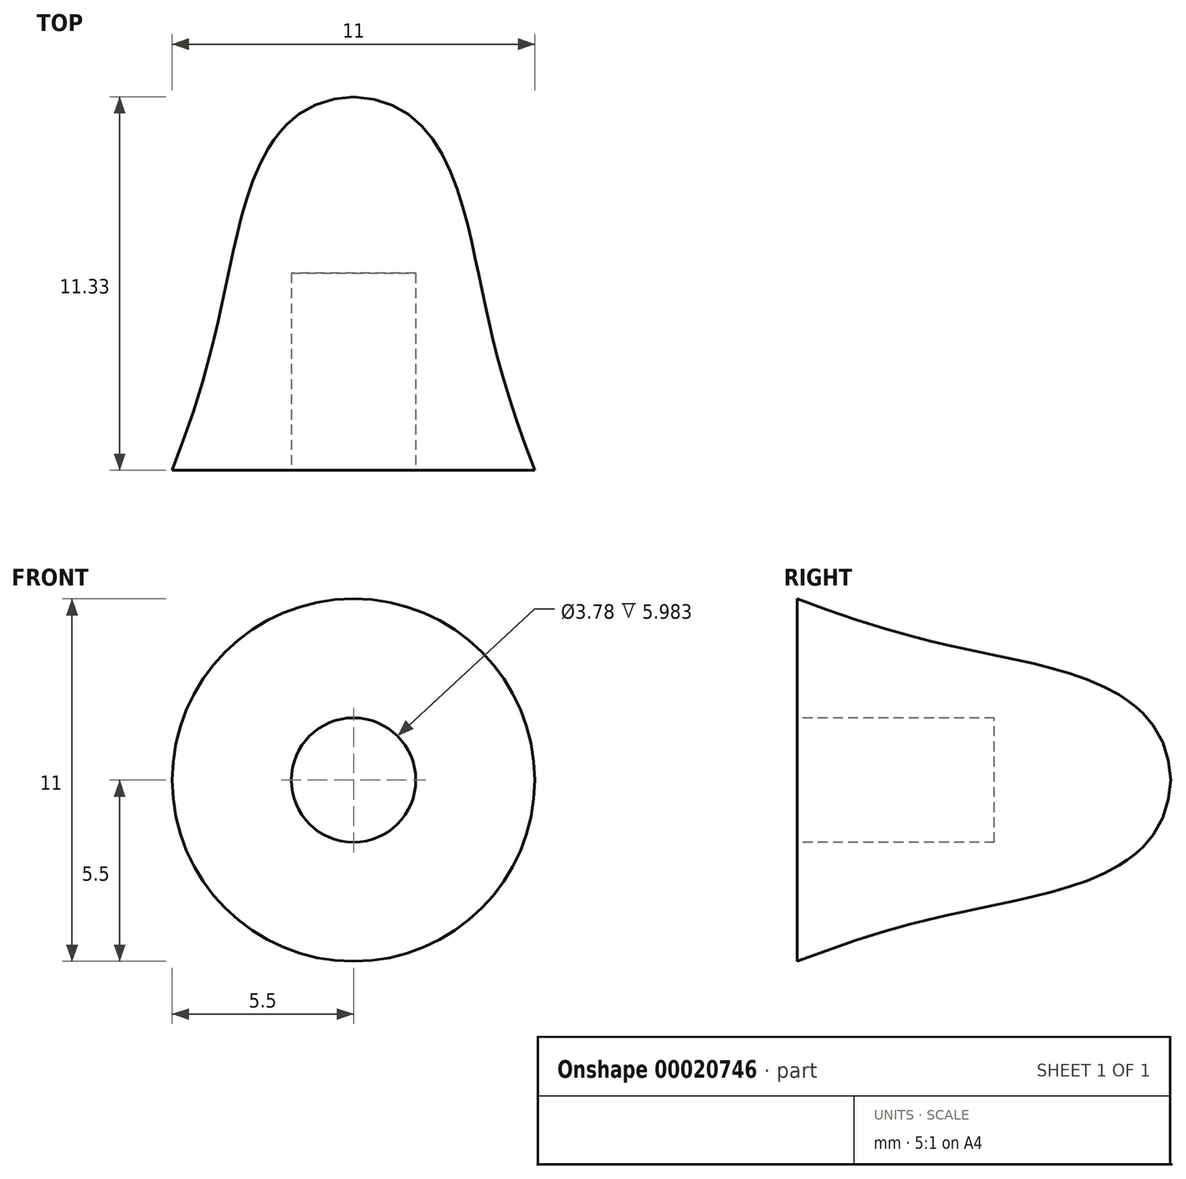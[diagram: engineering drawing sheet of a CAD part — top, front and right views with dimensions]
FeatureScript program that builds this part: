
annotation { "Feature Type Name" : "Feature", "Feature Type Description" : "" }
export const myFeature = defineFeature(function(context is Context, id is Id, definition is map)
    precondition{}
    {
        {
            var Q0;
            Q0=qCreatedBy(makeId("Top.planeOp"),FACE);
            var sketch = newSketch(context, id + "F0", { "sketchPlane" : qUnion([Q0])});
            skLineSegment(sketch, "E0.bottom", {"start": v(0, 0) * mm, "end": v(1.89, 0) * mm});
            skLineSegment(sketch, "E0.top", {"start": v(0, 5.98) * mm, "end": v(1.89, 5.98) * mm});
            skLineSegment(sketch, "E0.right", {"start": v(1.89, 0) * mm, "end": v(1.89, 5.98) * mm});
            skLineSegment(sketch, "E1.bottom", {"start": v(0, 0) * mm, "end": v(5.5, 0) * mm});
            skLineSegment(sketch, "E1.left", {"start": v(0, 5.98) * mm, "end": v(0, 11.33) * mm});
            skFitSpline(sketch, "E2", {"points": [v(0, 11.33) * mm, v(3.54, 7.13) * mm, v(5.5, 0) * mm], "startDerivative": vector(15.53, -0.48) * mm, "endDerivative": vector(7.33, -19.14) * mm});
            skSolve(sketch);
        }
        {
            var Q0;
            Q0=makeQuery(id+"F0.imprint","IMPRINT",FACE,{"disambiguationData":[TD([[makeQuery(id+"F0.imprint","IMPRINT",EDGE,{"derivedFrom":sQuery(id+"F0.wireOp",EDGE,"E0.top")}),1.0]])]});
            var Q1;
            Q1=sQuery(id+"F0.wireOp",EDGE,"E1.left");
            revolve(context, id + "F1", {"entities" : qUnion([Q0]), "axis" : qUnion([Q1]), "revolveType" : RevolveType.FULL});
        }
    });
